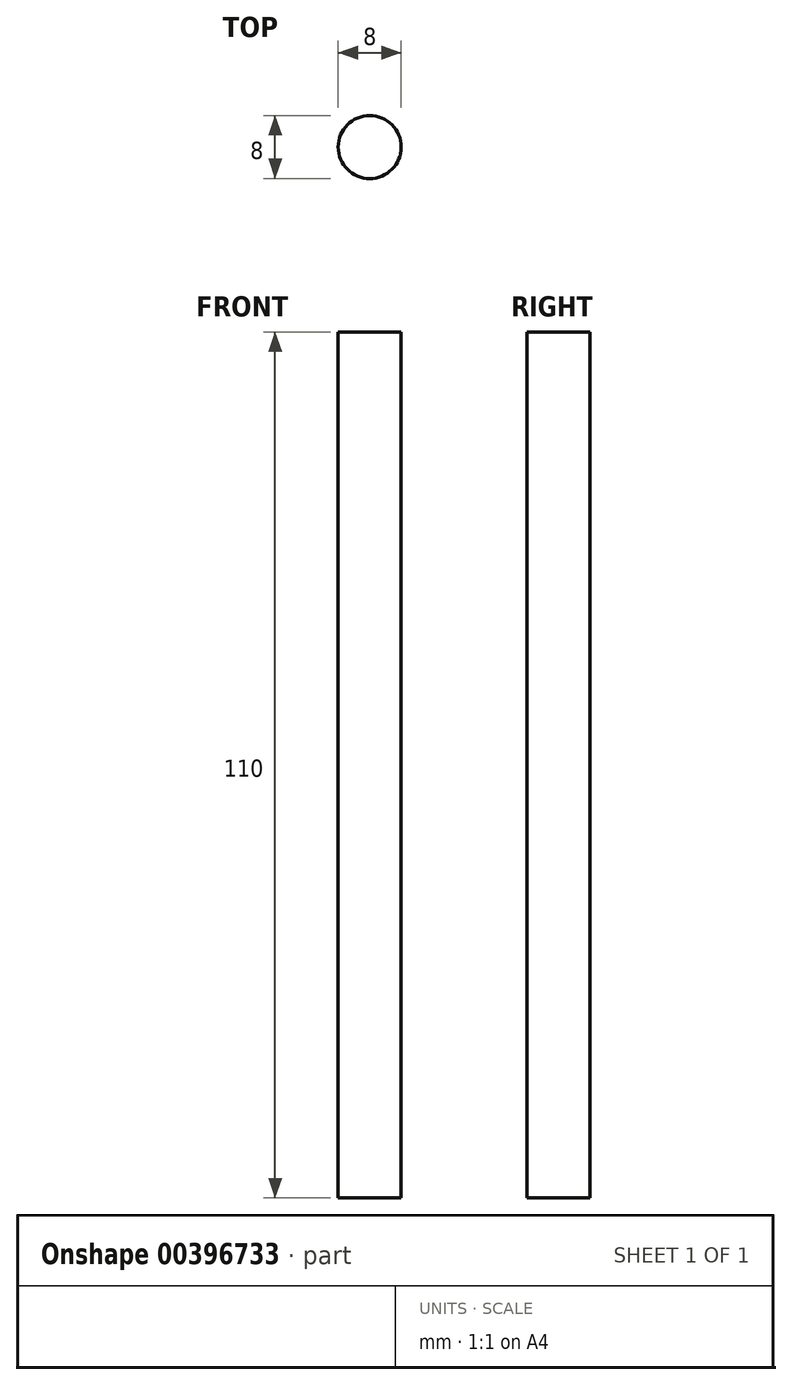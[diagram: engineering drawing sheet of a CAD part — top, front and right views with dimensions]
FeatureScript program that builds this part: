
annotation { "Feature Type Name" : "Feature", "Feature Type Description" : "" }
export const myFeature = defineFeature(function(context is Context, id is Id, definition is map)
    precondition{}
    {
        {
            var Q0;
            Q0=qCreatedBy(makeId("Top.planeOp"),FACE);
            var sketch = newSketch(context, id + "F0", { "sketchPlane" : qUnion([Q0])});
            skCircle(sketch, "E0", {"center": v(0, 0) * mm, "radius": 4 * mm});
            skSolve(sketch);
        }
        {
            var Q0;
            Q0=makeQuery(id+"F0.imprint","IMPRINT",FACE,{"disambiguationData":[TD([[makeQuery(id+"F0.imprint","IMPRINT",EDGE,{"derivedFrom":sQuery(id+"F0.wireOp",EDGE,"E0")}),1.0]])]});
            var Q1;
            Q1=sQuery(id+"F0.wireOp",EDGE,"E0");
            extrude(context, id + "F1", {"entities" : qUnion([Q0]), "surfaceEntities" : qUnion([Q1]), "depth" : 110 * mm});
        }
    });
